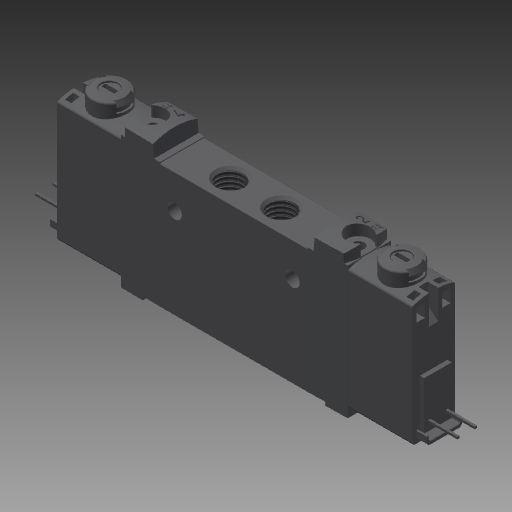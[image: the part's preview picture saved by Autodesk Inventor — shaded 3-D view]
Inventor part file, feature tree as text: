
AUTODESK INVENTOR PART (.ipt)
format: ipt  version: 2017.1 (Build 211199000, 199)  size: 724,480 bytes
history: native  units: mm
features: other x105, sketch x58, extrude x43, revolve x13, thread x3, hole x2
ambient origin geometry x8: Origin, YZ Plane, XZ Plane, XY Plane, X Axis, Y Axis, Z Axis, Center Point
bodies: Solid1 (feature_tree)
feature tree (224):
  extrude  "Extrusion1"  Depth=12.0mm TaperAngle=0.0deg
  extrude  "Extrusion2"  TaperAngle=360.0deg  [1 undecoded]
  extrude  "Extrusion3"  TaperAngle=360.0deg  [1 undecoded]
  sketch  "Sketch_5"  dims[d4=12.0mm d5=0.0mm d6=360.0deg]
  sketch  "Sketch_6"  dims[d7=5.4585mm d8=0.0mm d9=360.0deg]
  sketch  "Sketch_7"  dims[d10=5.4585mm d11=0.0mm d12=360.0deg d13=5.4585mm d14=0.0mm]
  revolve  "Revolution1"  Angle=360.0deg
  thread  "Thread1"  [1 undecoded]
  revolve  "Revolution2"  [1 undecoded]
  thread  "Thread2"  [1 undecoded]
  revolve  "Revolution3"  [1 undecoded]
  thread  "Thread3"  [1 undecoded]
  hole  "Hole1"  [1 undecoded]
  hole  "Hole2"  [1 undecoded]
  extrude  "Extrusion4"  Depth=4.0mm TaperAngle=0.0deg
  sketch  "Sketch_19"  dims[d43=7.7mm d44=0.0mm d45=7.7mm d46=0.0mm]
  extrude  "Extrusion5"  Depth=64.0mm TaperAngle=0.0deg
  extrude  "Extrusion6"  Depth=12.0mm TaperAngle=0.0deg
  extrude  "Extrusion7"  Depth=16.0mm TaperAngle=0.0deg
  extrude  "Extrusion8"  Depth=6.0mm TaperAngle=0.0deg
  extrude  "Extrusion9"  Depth=1.0mm TaperAngle=0.0deg
  extrude  "Extrusion10"  Depth=7.7mm TaperAngle=0.0deg
  extrude  "Extrusion11"  TaperAngle=360.0deg  [1 undecoded]
  extrude  "Extrusion12"  Depth=3.0mm TaperAngle=0.0deg
  revolve  "Revolution4"  Angle=360.0deg
  extrude  "Extrusion13"  TaperAngle=360.0deg  [1 undecoded]
  extrude  "Extrusion14"  TaperAngle=360.0deg  [1 undecoded]
  extrude  "Extrusion15"  Depth=2.15mm TaperAngle=0.0deg
  extrude  "Extrusion16"  Depth=2.1mm TaperAngle=0.0deg
  extrude  "Extrusion17"  Depth=1.5mm TaperAngle=0.0deg
  extrude  "Extrusion18"  Depth=3.0mm TaperAngle=0.0deg
  extrude  "Extrusion19"  Depth=3.0mm TaperAngle=0.0deg
  extrude  "Extrusion20"  Depth=2.0mm TaperAngle=0.0deg
  extrude  "Extrusion21"  Depth=2.0mm TaperAngle=0.0deg
  extrude  "Extrusion22"  Depth=2.0mm TaperAngle=0.0deg
  extrude  "Extrusion23"  TaperAngle=0.0deg  [1 undecoded]
  extrude  "Extrusion24"  [1 undecoded]
  extrude  "Extrusion25"  [1 undecoded]
  revolve  "Revolution5"  [1 undecoded]
  revolve  "Revolution6"  [1 undecoded]
  revolve  "Revolution7"  [1 undecoded]
  sketch  "Sketch_59"  dims[d97=1.5mm d98=0.0mm d99=3.0mm d100=0.0mm]
  sketch  "Sketch_56"  dims[d86=360.0deg d87=2.15mm d88=0.0mm]
  extrude  "Extrusion26"  [1 undecoded]
  extrude  "Extrusion27"  [1 undecoded]
  revolve  "Revolution8"  [1 undecoded]
  revolve  "Revolution9"  [1 undecoded]
  revolve  "Revolution10"  [1 undecoded]
  revolve  "Revolution11"  [1 undecoded]
  revolve  "Revolution12"  [1 undecoded]
  revolve  "Revolution13"  [1 undecoded]
  extrude  "Extrusion28"  [1 undecoded]
  extrude  "Extrusion29"  [1 undecoded]
  extrude  "Extrusion30"  [1 undecoded]
  extrude  "Extrusion31"  [1 undecoded]
  extrude  "Extrusion32"  [1 undecoded]
  extrude  "Extrusion33"  [1 undecoded]
  extrude  "Extrusion34"  [1 undecoded]
  extrude  "Extrusion35"  [1 undecoded]
  extrude  "Extrusion36"  [1 undecoded]
  extrude  "Extrusion37"  [1 undecoded]
  extrude  "Extrusion38"  [1 undecoded]
  extrude  "Extrusion39"  [1 undecoded]
  extrude  "Extrusion40"  [1 undecoded]
  extrude  "Extrusion41"  [1 undecoded]
  extrude  "Extrusion42"  [1 undecoded]
  extrude  "Extrusion43"  [1 undecoded]
  other  "DICHTUNG_XY"
  other  "DICHTUNG_YZ"
  other  "DICHTUNG_ZX"
  other  "DICHTUNG_X"
  other  "DICHTUNG_Y"
  other  "DICHTUNG_Z"
  other  "DICHTUNG_Center"
  other  "GEHAUSE_XY"
  other  "GEHAUSE_YZ"
  other  "GEHAUSE_ZX"
  other  "GEHAUSE_X"
  other  "GEHAUSE_Y"
  other  "GEHAUSE_Z"
  other  "GEHAUSE_Center"
  other  "HHB1_XY"
  other  "HHB1_YZ"
  other  "HHB1_ZX"
  other  "HHB1_X"
  other  "HHB1_Y"
  other  "HHB1_Z"
  other  "HHB1_Center"
  other  "HHB2_XY"
  other  "HHB2_YZ"
  other  "HHB2_ZX"
  other  "HHB2_X"
  other  "HHB2_Y"
  other  "HHB2_Z"
  other  "HHB2_Center"
  other  "NEBV1_XY"
  other  "NEBV1_YZ"
  other  "NEBV1_ZX"
  other  "NEBV1_X"
  other  "NEBV1_Y"
  other  "NEBV1_Z"
  other  "NEBV1_Center"
  other  "NEBV2_XY"
  other  "NEBV2_YZ"
  other  "NEBV2_ZX"
  other  "NEBV2_X"
  other  "NEBV2_Y"
  other  "NEBV2_Z"
  other  "NEBV2_Center"
  other  "QS1_XY"
  other  "QS1_YZ"
  other  "QS1_ZX"
  other  "QS1_X"
  other  "QS1_Y"
  other  "QS1_Z"
  other  "QS1_Center"
  other  "QS2_XY"
  other  "QS2_YZ"
  other  "QS2_ZX"
  other  "QS2_X"
  other  "QS2_Y"
  other  "QS2_Z"
  other  "QS2_Center"
  other  "QSZ_XY"
  other  "QSZ_YZ"
  other  "QSZ_ZX"
  other  "QSZ_X"
  other  "QSZ_Y"
  other  "QSZ_Z"
  other  "QSZ_Center"
  other  "SCREW1_XY"
  other  "SCREW1_YZ"
  other  "SCREW1_ZX"
  other  "SCREW1_X"
  other  "SCREW1_Y"
  other  "SCREW1_Z"
  other  "SCREW1_Center"
  other  "SCREW2_XY"
  other  "SCREW2_YZ"
  other  "SCREW2_ZX"
  other  "SCREW2_X"
  other  "SCREW2_Y"
  other  "SCREW2_Z"
  other  "SCREW2_Center"
  other  "U1_XY"
  other  "U1_YZ"
  other  "U1_ZX"
  other  "U1_X"
  other  "U1_Y"
  other  "U1_Z"
  other  "U1_Center"
  other  "U2_XY"
  other  "U2_YZ"
  other  "U2_ZX"
  other  "U2_X"
  other  "U2_Y"
  other  "U2_Z"
  other  "U2_Center"
  other  "VAVE1_XY"
  other  "VAVE1_YZ"
  other  "VAVE1_ZX"
  other  "VAVE1_X"
  other  "VAVE1_Y"
  other  "VAVE1_Z"
  other  "VAVE1_Center"
  other  "VAVE2_XY"
  other  "VAVE2_YZ"
  other  "VAVE2_ZX"
  other  "VAVE2_X"
  other  "VAVE2_Y"
  other  "VAVE2_Z"
  other  "VAVE2_Center"
  sketch  "Sketch_53"  dims[d84=360.0deg d85=360.0deg]
  sketch  "Sketch_143"
  sketch  "Sketch_142"
  sketch  "Sketch7"  dims[d15=5.917468mm d16=6.5415mm d17=7.0mm d18=2.0mm d19=90.0deg d20=6.8mm d21=0.0mm]
  sketch  "Sketch8"  dims[d22=5.917468mm d23=6.5415mm d24=7.0mm d25=2.0mm d26=90.0deg d27=6.8mm d28=0.0mm d29=33.1mm d30=0.0mm d31=5.0mm d32=0.0mm]
  sketch  "Sketch_17"  dims[d39=2.4mm d40=0.0mm d41=1.0mm d42=0.0mm]
  sketch  "Sketch_30"  dims[d58=5.0mm d59=0.0mm d60=16.0mm d61=0.0mm]
  sketch  "Sketch_22"  dims[d50=33.1mm d51=0.0mm d52=64.0mm d53=0.0mm]
  sketch  "Sketch_23"  dims[d54=4.0mm d55=0.0mm d56=12.0mm d57=0.0mm]
  sketch  "Sketch_120"
  sketch  "Sketch_126"
  sketch  "Sketch_123"
  sketch  "Sketch_124"
  sketch  "Sketch_125"
  sketch  "Sketch_21"  dims[d47=360.0deg d48=4.0mm d49=0.0mm]
  sketch  "Sketch_31"  dims[d62=21.34mm d63=0.0mm d64=6.0mm d65=0.0mm]
  sketch  "Sketch_32"  dims[d66=2.4mm d67=0.0mm d68=1.0mm d69=0.0mm]
  sketch  "Sketch_119"
  sketch  "Sketch_36"  dims[d76=360.0deg d77=3.0mm d78=0.0mm]
  sketch  "Sketch_37"  dims[d79=3.0mm d80=0.0mm d81=360.0deg]
  sketch  "Sketch_35"  dims[d74=360.0deg d75=360.0deg]
  sketch  "Sketch_38"  dims[d82=360.0deg d83=360.0deg]
  sketch  "Sketch_127"
  sketch  "Sketch_128"
  sketch  "Sketch_129"
  sketch  "Sketch_130"
  sketch  "Sketch_131"
  sketch  "Sketch_34"  dims[d70=7.7mm d71=0.0mm d72=7.7mm d73=0.0mm]
  sketch  "Sketch_4"  dims[d0=33.8mm d1=0.0mm d2=12.0mm d3=0.0mm]
  sketch  "Sketch_61"  dims[d105=3.0mm d106=0.0mm d107=2.0mm d108=0.0mm]
  sketch  "Sketch_57"  dims[d89=2.15mm d90=0.0mm d91=2.1mm d92=0.0mm]
  sketch  "Sketch_62"  dims[d109=2.0mm d110=0.0mm d111=2.0mm d112=0.0mm]
  sketch  "Sketch_58"  dims[d93=2.1mm d94=0.0mm d95=1.5mm d96=0.0mm]
  sketch  "Sketch_63"  dims[d113=2.0mm d114=0.0mm d115=2.0mm d116=0.0mm]
  sketch  "Sketch_64"  dims[d117=2.0mm d118=0.0mm d119=0.0mm d120=0.0mm d121=0.0mm d122=0.0mm]
  sketch  "Sketch_65"
  sketch  "Sketch_60"  dims[d101=3.0mm d102=0.0mm d103=3.0mm d104=0.0mm]
  sketch  "Sketch_66"
  sketch  "Sketch_84"
  sketch  "Sketch_81"
  sketch  "Sketch_132"
  sketch  "Sketch_133"
  sketch  "Sketch_134"
  sketch  "Sketch_135"
  sketch  "Sketch_136"
  sketch  "Sketch_137"
  sketch  "Sketch_12"  dims[d33=12.0mm d34=0.0mm d35=21.34mm d36=0.0mm d37=3.0mm d38=0.0mm]
  sketch  "Sketch_68"
  sketch  "Sketch_101"
  sketch  "Sketch_102"
  sketch  "Sketch_103"
  sketch  "Sketch_104"
note: 42 required parameter values undecoded (feature->parameter linkage not recoverable at this tier; creation-order binding heuristic only, values carry confidence <= 0.55)